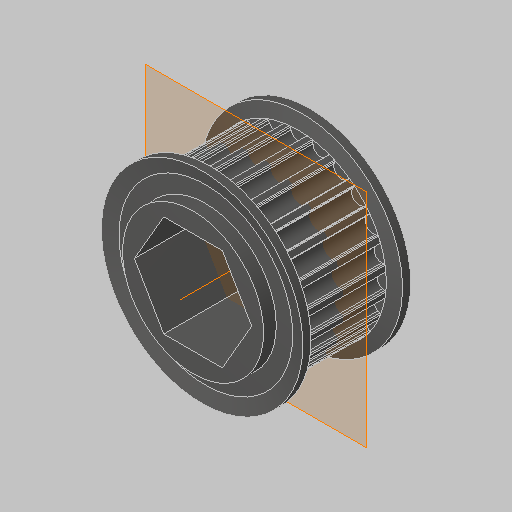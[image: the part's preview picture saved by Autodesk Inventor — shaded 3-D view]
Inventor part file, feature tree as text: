
AUTODESK INVENTOR PART (.ipt)
format: ipt  version: 2023.5 (Build 275446000, 446)  size: 332,288 bytes
history: native  units: in
note: dims shown in document units (in); Inventor stores cm internally (conversion verified against a paired STEP export)
features: other x1, plane x1, mirror x1
ambient origin geometry x8: Origin, YZ Plane, XZ Plane, XY Plane, X Axis, Y Axis, Z Axis, Center Point
bodies: Solid1 (feature_tree)
feature tree (3):
  other  "Work Axis1"
  plane  "Work Plane1"
  mirror  "Mirror1"
